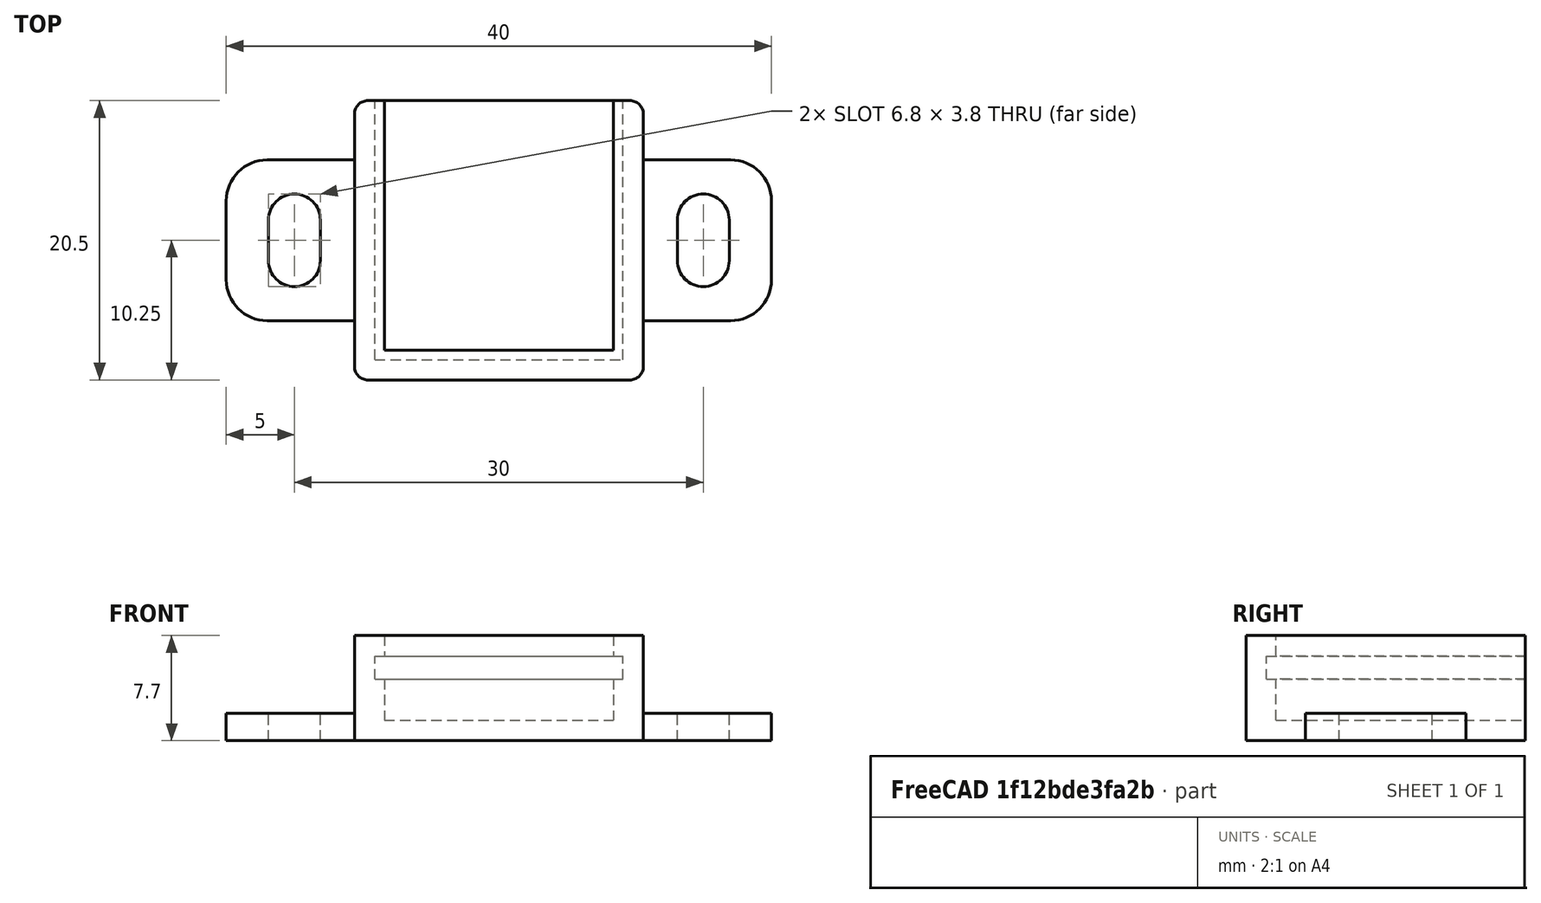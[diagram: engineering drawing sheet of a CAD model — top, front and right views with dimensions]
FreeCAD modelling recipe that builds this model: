
FCSTD DOCUMENT  (FreeCAD 0.19R)
Label: micro_sd
License: FreeArt
LicenseURL: http://artlibre.org/licence/lal
objects: Part::Box×3, Part::MultiFuse×2, Part::Cut×2, App::Part×2, Spreadsheet::Sheet×1, Part::Fillet×1, Part::Feature×1
note: 9 computed .brp shape members not serialized (recipe doc carries the construction recipe); baked Part::Feature solids carry a one-line shape summary decoded from their .brp

FEATURE [Spreadsheet::Sheet] Spreadsheet  label="p"
  cells = A1=pcb_x; B1(pcb_x)=18.2; A2=pcb_y; B2(pcb_y)=19; A3=pcb_z; B3(pcb_z)=1.7; A4=pcb_under; B4(pcb_under)=3; A5=side_wall; B5(side_wall)=1.5; A6=pcb_side_lane; B6(pcb_side_lane)=0.7; A7=bottom_wall; B7(bottom_wall)=1.5; A8=pcb_above; B8(pcb_above)=1.5; A9=hole_dist_x; B9(hole_dist_x)=14.5; A10=hole_r; B10(hole_r)=0.6; A11=hole_off_y; B11(hole_off_y)=5; A12=hole_stand_size; B12(hole_stand_size)=6
FEATURE [Part::Box] Box  label="external cube"
  AttacherType = Attacher::AttachEngine3D
  Height = 7.7
  Length = 21.2
  Width = 20.5
  expr: Height = <<p>>.bottom_wall + <<p>>.pcb_under + <<p>>.pcb_z + <<p>>.pcb_above
  expr: Width = <<p>>.pcb_y + <<p>>.side_wall
  expr: Length = <<p>>.pcb_x + 2 * <<p>>.side_wall
FEATURE [Part::Box] Box006  label="internal cube"
  AttacherType = Attacher::AttachEngine3D
  Height = 6.2
  Length = 16.8
  Placement = pos=(2.2,2.2,1.5) rot=(0,0,1;0rad)
  Width = 19.1
  expr: .Placement.Base.y = <<p>>.side_wall + <<p>>.pcb_side_lane
  expr: .Placement.Base.x = <<p>>.side_wall + <<p>>.pcb_side_lane
  expr: .Placement.Base.z = <<p>>.bottom_wall
  expr: Height = <<p>>.pcb_under + <<p>>.pcb_z + <<p>>.pcb_above
  expr: Width = <<p>>.pcb_y - 2 * <<p>>.pcb_side_lane + <<p>>.side_wall
  expr: Length = <<p>>.pcb_x - 2 * <<p>>.pcb_side_lane
FEATURE [Part::Box] Box007  label="pcb extract cube"
  AttacherType = Attacher::AttachEngine3D
  Height = 1.7
  Length = 18.2
  Placement = pos=(1.5,1.5,4.5) rot=(0,0,1;0rad)
  Width = 19
  expr: .Placement.Base.y = <<p>>.side_wall
  expr: .Placement.Base.x = <<p>>.side_wall
  expr: Length = <<p>>.pcb_x
  expr: Width = <<p>>.pcb_y
  expr: .Placement.Base.z = <<p>>.bottom_wall + <<p>>.pcb_under
  expr: Height = <<p>>.pcb_z
FEATURE [Part::MultiFuse] Fusion  label="extract fusion"
  Shapes = -> [Box006,Box007]
FEATURE [Part::Fillet] Fillet  label="external fillet"
  Base = -> Box
  Edges = 4 edges r=1: [Edge1,Edge3,Edge5,Edge7]
FEATURE [Part::Feature] Cut003001  label="attach plane x dir001"
  Placement = pos=(-9.4,4.35,0) rot=(0,0,1;0rad)
  shape: bbox 40 x 11.8 x 2 mm, 18 faces (baked)
FEATURE [Part::MultiFuse] Fusion001  label="body fusion"
  Shapes = -> [Fillet,Cut003001]
FEATURE [Part::Cut] Cut  label="body cut"
  Base = -> Fusion001
  Tool = -> Fusion
FEATURE [App::Part] Part  label="micro sd pcb box part"
  Group = -> [Box,Fillet,Fusion001,Fusion,Box007,Box006,Cut]
  Origin = -> Origin
FEATURE [Part::Cut] Cut003002  label="body cut001"
  Base = -> Fillet
  Tool = -> Fusion
FEATURE [App::Part] Part001  label="micro sd pcb box part001"
  Group = -> [Cut003002]
  Origin = -> Origin001
